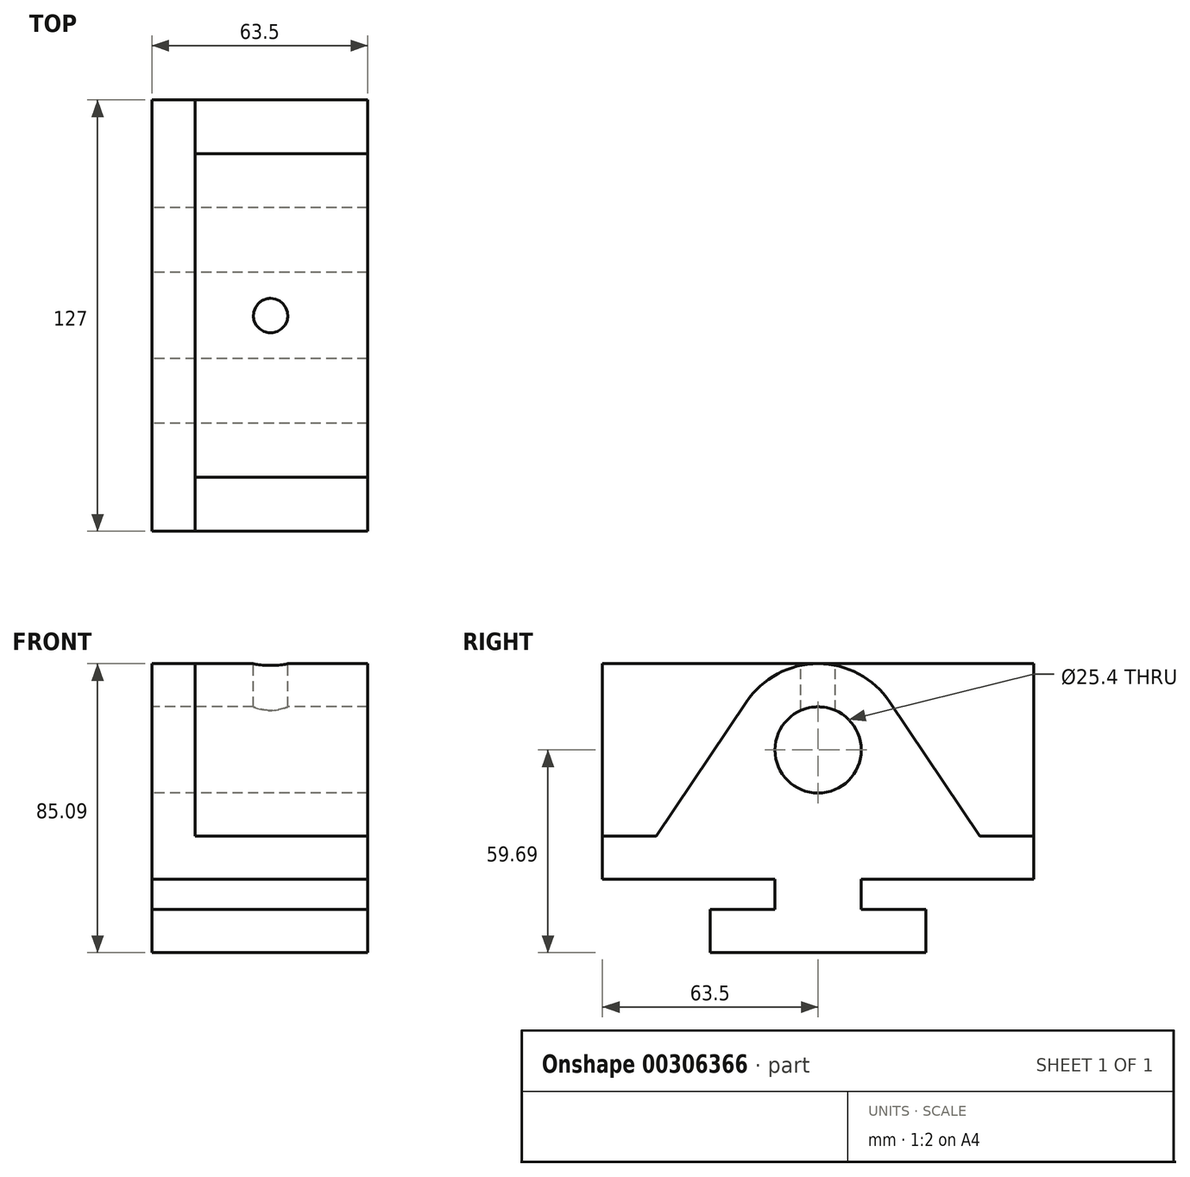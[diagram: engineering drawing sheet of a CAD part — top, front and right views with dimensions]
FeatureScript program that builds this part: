
annotation { "Feature Type Name" : "Feature", "Feature Type Description" : "" }
export const myFeature = defineFeature(function(context is Context, id is Id, definition is map)
    precondition{}
    {
        {
            var Q0;
            Q0=qCreatedBy(makeId("Front.planeOp"),FACE);
            var sketch = newSketch(context, id + "F0", { "sketchPlane" : qUnion([Q0])});
            skLineSegment(sketch, "E0.bottom", {"start": v(31.75, 0) * mm, "end": v(95.25, 0) * mm});
            skLineSegment(sketch, "E0.top", {"start": v(0, 85.1) * mm, "end": v(127, 85.1) * mm});
            skLineSegment(sketch, "E0.left", {"start": v(0, 21.59) * mm, "end": v(0, 85.1) * mm});
            skLineSegment(sketch, "E0.right", {"start": v(127, 21.59) * mm, "end": v(127, 85.1) * mm});
            skCircle(sketch, "E1", {"center": v(63.5, 59.7) * mm, "radius": 12.7 * mm});
            skPoint(sketch, "E1.centerSnap0", {"position": v(63.5, 85.1) * mm});
            skArc(sketch, "E2", {"start": v(84.6, 73.84) * mm, "mid": v(63.5, 85.1) * mm, "end": v(42.4, 73.84) * mm});
            skLineSegment(sketch, "E3", {"start": v(127, 34.3) * mm, "end": v(111.12, 34.3) * mm});
            skLineSegment(sketch, "E4", {"start": v(0, 34.3) * mm, "end": v(15.87, 34.3) * mm});
            skLineSegment(sketch, "E5", {"start": v(15.88, 34.3) * mm, "end": v(42.4, 73.84) * mm});
            skLineSegment(sketch, "E6", {"start": v(111.12, 34.3) * mm, "end": v(84.6, 73.84) * mm});
            skLineSegment(sketch, "E7", {"start": v(0, 21.59) * mm, "end": v(50.8, 21.59) * mm});
            skLineSegment(sketch, "E8", {"start": v(95.25, 0) * mm, "end": v(95.25, 12.7) * mm});
            skLineSegment(sketch, "E9", {"start": v(31.75, 0) * mm, "end": v(31.75, 12.7) * mm});
            skPoint(sketch, "E10", {"position": v(50.8, 59.7) * mm});
            skPoint(sketch, "E11", {"position": v(76.2, 59.7) * mm});
            skLineSegment(sketch, "E12", {"start": v(31.75, 12.7) * mm, "end": v(50.8, 12.7) * mm});
            skLineSegment(sketch, "E13", {"start": v(95.25, 12.7) * mm, "end": v(76.2, 12.7) * mm});
            skLineSegment(sketch, "E14", {"start": v(50.8, 12.7) * mm, "end": v(50.8, 21.59) * mm});
            skLineSegment(sketch, "E15", {"start": v(76.2, 12.7) * mm, "end": v(76.2, 21.59) * mm});
            skLineSegment(sketch, "E16.trimOffspring", {"start": v(76.2, 21.59) * mm, "end": v(127, 21.59) * mm});
            skPoint(sketch, "E17.orphan", {"position": v(0, 0) * mm});
            skSolve(sketch);
        }
        {
            var Q0;
            Q0=makeQuery(id+"F0.imprint","IMPRINT",FACE,{"disambiguationData":[TD([[makeQuery(id+"F0.imprint","IMPRINT",EDGE,{"derivedFrom":sQuery(id+"F0.wireOp",EDGE,"E0.bottom")}),1.0]])]});
            extrude(context, id + "F1", {"entities" : qUnion([Q0]), "depth" : 50.8 * mm});
        }
        {
            var Q0;
            Q0 = qSketchRegion(id + "F0", true);
            extrude(context, id + "F2", {"entities" : qUnion([Q0]), "operationType" : NewBodyOperationType.ADD, "oppositeDirection" : true, "depth" : 12.7 * mm});
        }
        {
            var Q0;
            Q0=makeQuery(id+"F2.opExtrude","SWEPT_FACE",FACE,{"disambiguationData":[OSD([sQuery(id+"F0.wireOp",EDGE,"E0.top")])]});
            var sketch = newSketch(context, id + "F3", { "sketchPlane" : qUnion([Q0])});
            skCircle(sketch, "E18", {"center": v(63.5, -22.23) * mm, "radius": 5.08 * mm});
            skSolve(sketch);
        }
        {
            var Q0;
            Q0 = qSketchRegion(id + "F3", true);
            extrude(context, id + "F4", {"entities" : qUnion([Q0]), "operationType" : NewBodyOperationType.REMOVE, "endBound" : BoundingType.UP_TO_NEXT, "oppositeDirection" : true, "depth" : 6.35 * mm});
        }
        {
            var Q0;
            Q0=makeQuery(id+"F1.opExtrude","SWEPT_BODY",BODY,{"disambiguationData":[OSD([sQuery(id+"F0.wireOp",EDGE,"E0.bottom"),sQuery(id+"F0.wireOp",EDGE,"E0.left"),sQuery(id+"F0.wireOp",EDGE,"E0.right"),sQuery(id+"F0.wireOp",EDGE,"E1"),sQuery(id+"F0.wireOp",EDGE,"E2"),sQuery(id+"F0.wireOp",EDGE,"E3"),sQuery(id+"F0.wireOp",EDGE,"E4"),sQuery(id+"F0.wireOp",EDGE,"E5"),sQuery(id+"F0.wireOp",EDGE,"E6"),sQuery(id+"F0.wireOp",EDGE,"E7"),sQuery(id+"F0.wireOp",EDGE,"E8"),sQuery(id+"F0.wireOp",EDGE,"E9"),sQuery(id+"F0.wireOp",EDGE,"E12"),sQuery(id+"F0.wireOp",EDGE,"E13"),sQuery(id+"F0.wireOp",EDGE,"E14"),sQuery(id+"F0.wireOp",EDGE,"E15"),sQuery(id+"F0.wireOp",EDGE,"E16.trimOffspring")])]});
            var Q1;
            Q1=makeQuery(id+"F2.opExtrude","CAP_EDGE",EDGE,{"disambiguationData":[OSD([sQuery(id+"F0.wireOp",EDGE,"E0.left")])],"isStart":true});
            transform(context, id + "F5", {"entities" : qUnion([Q0]), "transformType" : TransformType.ROTATION, "transformAxis" : qUnion([Q1]), "angle" : 90 * degree, "makeCopy" : false});
        }
    });
